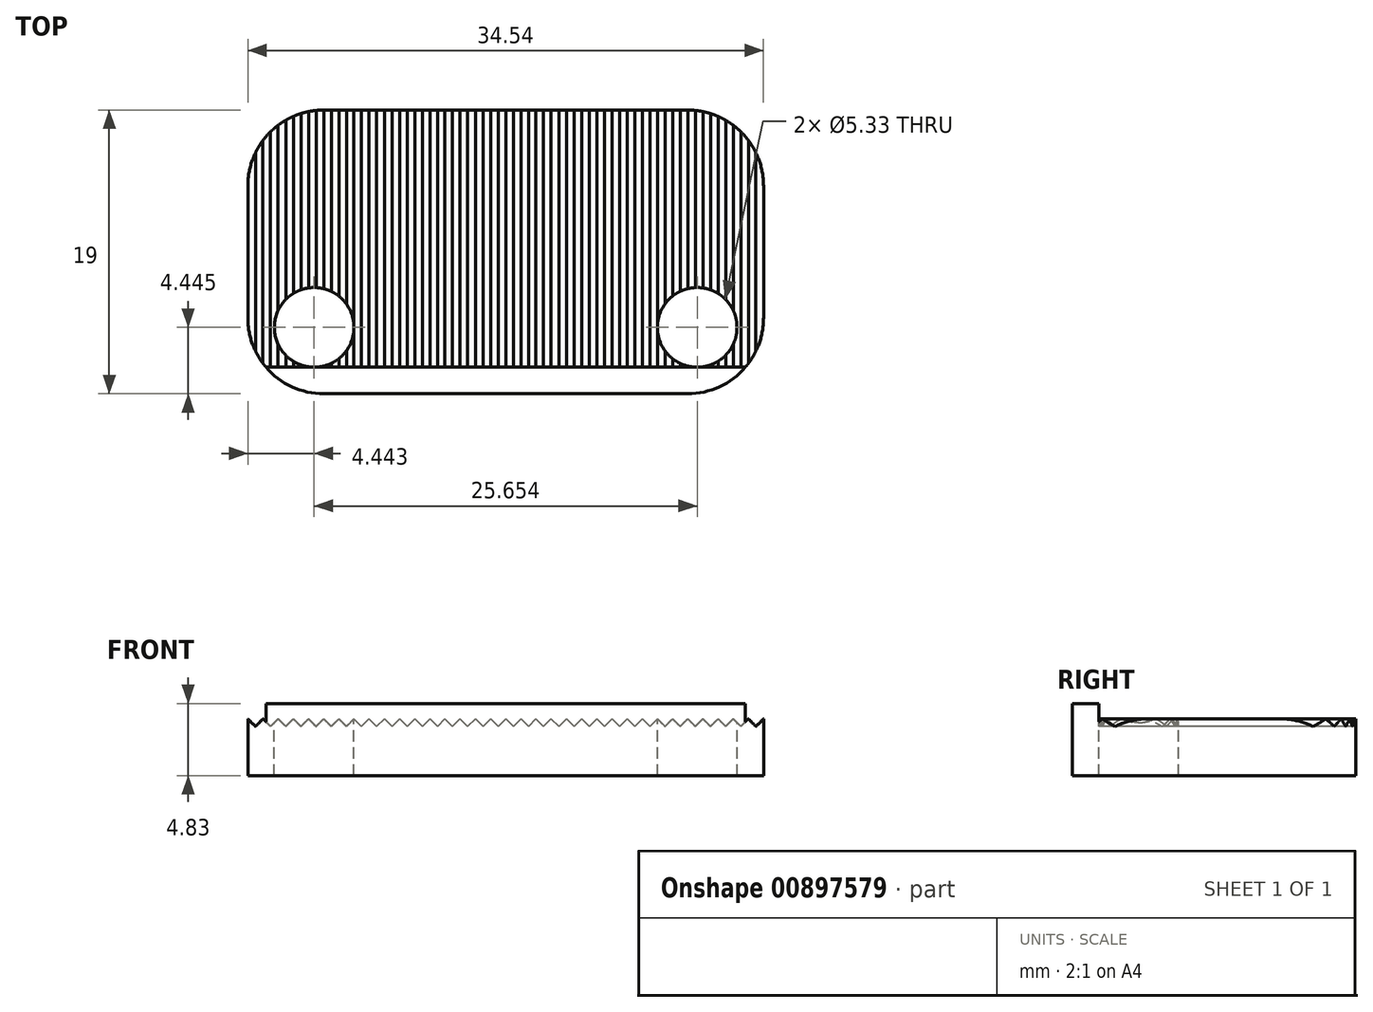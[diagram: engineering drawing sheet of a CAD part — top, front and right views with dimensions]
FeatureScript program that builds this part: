
annotation { "Feature Type Name" : "Feature", "Feature Type Description" : "" }
export const myFeature = defineFeature(function(context is Context, id is Id, definition is map)
    precondition{}
    {
        {
            var Q0;
            Q0=qCreatedBy(makeId("Top.planeOp"),FACE);
            var sketch = newSketch(context, id + "F0", { "sketchPlane" : qUnion([Q0])});
            skLineSegment(sketch, "E0.bottom", {"start": v(17.27, -9.5) * mm, "end": v(-17.27, -9.5) * mm});
            skLineSegment(sketch, "E0.top", {"start": v(17.27, 9.5) * mm, "end": v(-17.27, 9.5) * mm});
            skLineSegment(sketch, "E0.left", {"start": v(17.27, -9.5) * mm, "end": v(17.27, 9.5) * mm});
            skLineSegment(sketch, "E0.right", {"start": v(-17.27, -9.5) * mm, "end": v(-17.27, 9.5) * mm});
            skPoint(sketch, "E0.middle", {"position": v(0, 0) * mm});
            skSolve(sketch);
        }
        {
            var Q0;
            Q0=qSketchRegion(id+"F0",true);
            extrude(context, id + "F1", {"entities" : qUnion([Q0]), "depth" : 3.8 * mm, "offsetDistance" : 25.4 * mm});
        }
        {
            var Q0;
            Q0=makeQuery(id+"F1.opExtrude","SWEPT_FACE",FACE,{"disambiguationData":[OSD([sQuery(id+"F0.wireOp",EDGE,"E0.bottom")])]});
            var sketch = newSketch(context, id + "F2", { "sketchPlane" : qUnion([Q0])});
            skLineSegment(sketch, "E1", {"start": v(-16.27, 3.8) * mm, "end": v(-16.27, 3.06) * mm});
            skLineSegment(sketch, "E2", {"start": v(-16.27, 3.06) * mm, "end": v(-15.27, 3.06) * mm});
            skLineSegment(sketch, "E3", {"start": v(-15.27, 3.06) * mm, "end": v(-15.27, 3.8) * mm});
            skSolve(sketch);
        }
        {
            var Q0;
            Q0=makeQuery(id+"F1.opExtrude","CAP_FACE",FACE,{"disambiguationData":[OSD([sQuery(id+"F0.wireOp",EDGE,"E0.bottom"),sQuery(id+"F0.wireOp",EDGE,"E0.top"),sQuery(id+"F0.wireOp",EDGE,"E0.left"),sQuery(id+"F0.wireOp",EDGE,"E0.right")])],"isStart":false});
            var sketch = newSketch(context, id + "F3", { "sketchPlane" : qUnion([Q0])});
            skCircle(sketch, "E4", {"center": v(-12.83, -5.06) * mm, "radius": 2.67 * mm});
            skCircle(sketch, "E5", {"center": v(12.83, -5.06) * mm, "radius": 2.67 * mm});
            skSolve(sketch);
        }
        {
            var Q0;
            Q0=qSketchRegion(id+"F3",true);
            extrude(context, id + "F4", {"entities" : qUnion([Q0]), "operationType" : NewBodyOperationType.REMOVE, "oppositeDirection" : true, "depth" : 10.16 * mm, "offsetDistance" : 25.4 * mm});
        }
        {
            var Q0;
            Q0=makeQuery(id+"F1.opExtrude","SWEPT_FACE",FACE,{"disambiguationData":[OSD([sQuery(id+"F0.wireOp",EDGE,"E0.bottom")])]});
            var sketch = newSketch(context, id + "F5", { "sketchPlane" : qUnion([Q0])});
            skLineSegment(sketch, "E6", {"start": v(17.27, 3.8) * mm, "end": v(16.76, 3.3) * mm});
            skLineSegment(sketch, "E7", {"start": v(16.76, 3.3) * mm, "end": v(16.26, 3.81) * mm});
            skLineSegment(sketch, "E8.1.0.0", {"start": v(16.26, 3.8) * mm, "end": v(15.75, 3.3) * mm});
            skLineSegment(sketch, "E8.1.0.1", {"start": v(15.75, 3.3) * mm, "end": v(15.24, 3.81) * mm});
            skLineSegment(sketch, "E8.2.0.0", {"start": v(15.24, 3.81) * mm, "end": v(14.73, 3.3) * mm});
            skLineSegment(sketch, "E8.2.0.1", {"start": v(14.73, 3.3) * mm, "end": v(14.22, 3.81) * mm});
            skLineSegment(sketch, "E8.3.0.0", {"start": v(14.22, 3.8) * mm, "end": v(13.72, 3.3) * mm});
            skLineSegment(sketch, "E8.3.0.1", {"start": v(13.72, 3.3) * mm, "end": v(13.2, 3.81) * mm});
            skLineSegment(sketch, "E8.4.0.0", {"start": v(13.2, 3.8) * mm, "end": v(12.7, 3.3) * mm});
            skLineSegment(sketch, "E8.4.0.1", {"start": v(12.7, 3.3) * mm, "end": v(12.2, 3.81) * mm});
            skLineSegment(sketch, "E8.5.0.0", {"start": v(12.2, 3.8) * mm, "end": v(11.68, 3.3) * mm});
            skLineSegment(sketch, "E8.5.0.1", {"start": v(11.68, 3.3) * mm, "end": v(11.18, 3.81) * mm});
            skLineSegment(sketch, "E8.6.0.0", {"start": v(11.18, 3.8) * mm, "end": v(10.67, 3.3) * mm});
            skLineSegment(sketch, "E8.6.0.1", {"start": v(10.67, 3.3) * mm, "end": v(10.16, 3.81) * mm});
            skLineSegment(sketch, "E8.7.0.0", {"start": v(10.16, 3.8) * mm, "end": v(9.65, 3.3) * mm});
            skLineSegment(sketch, "E8.7.0.1", {"start": v(9.65, 3.3) * mm, "end": v(9.14, 3.81) * mm});
            skLineSegment(sketch, "E8.8.0.0", {"start": v(9.14, 3.8) * mm, "end": v(8.64, 3.3) * mm});
            skLineSegment(sketch, "E8.8.0.1", {"start": v(8.64, 3.3) * mm, "end": v(8.13, 3.81) * mm});
            skLineSegment(sketch, "E8.9.0.0", {"start": v(8.13, 3.8) * mm, "end": v(7.62, 3.3) * mm});
            skLineSegment(sketch, "E8.9.0.1", {"start": v(7.62, 3.3) * mm, "end": v(7.11, 3.81) * mm});
            skLineSegment(sketch, "E8.10.0.0", {"start": v(7.11, 3.8) * mm, "end": v(6.6, 3.3) * mm});
            skLineSegment(sketch, "E8.10.0.1", {"start": v(6.6, 3.3) * mm, "end": v(6.1, 3.81) * mm});
            skLineSegment(sketch, "E8.11.0.0", {"start": v(6.1, 3.8) * mm, "end": v(5.59, 3.3) * mm});
            skLineSegment(sketch, "E8.11.0.1", {"start": v(5.59, 3.3) * mm, "end": v(5.08, 3.81) * mm});
            skLineSegment(sketch, "E8.12.0.0", {"start": v(5.08, 3.8) * mm, "end": v(4.57, 3.3) * mm});
            skLineSegment(sketch, "E8.12.0.1", {"start": v(4.57, 3.3) * mm, "end": v(4.06, 3.81) * mm});
            skLineSegment(sketch, "E8.13.0.0", {"start": v(4.06, 3.8) * mm, "end": v(3.56, 3.3) * mm});
            skLineSegment(sketch, "E8.13.0.1", {"start": v(3.56, 3.3) * mm, "end": v(3.05, 3.81) * mm});
            skLineSegment(sketch, "E8.14.0.0", {"start": v(3.05, 3.8) * mm, "end": v(2.54, 3.3) * mm});
            skLineSegment(sketch, "E8.14.0.1", {"start": v(2.54, 3.3) * mm, "end": v(2.03, 3.81) * mm});
            skLineSegment(sketch, "E8.15.0.0", {"start": v(2.03, 3.8) * mm, "end": v(1.52, 3.3) * mm});
            skLineSegment(sketch, "E8.15.0.1", {"start": v(1.52, 3.3) * mm, "end": v(1.02, 3.8) * mm});
            skLineSegment(sketch, "E8.16.0.0", {"start": v(1.02, 3.8) * mm, "end": v(0.5, 3.3) * mm});
            skLineSegment(sketch, "E8.16.0.1", {"start": v(0.5, 3.3) * mm, "end": v(0, 3.81) * mm});
            skLineSegment(sketch, "E8.17.0.0", {"start": v(0, 3.8) * mm, "end": v(-0.5, 3.3) * mm});
            skLineSegment(sketch, "E8.17.0.1", {"start": v(-0.5, 3.3) * mm, "end": v(-1.02, 3.81) * mm});
            skLineSegment(sketch, "E8.18.0.0", {"start": v(-1.02, 3.8) * mm, "end": v(-1.52, 3.3) * mm});
            skLineSegment(sketch, "E8.18.0.1", {"start": v(-1.52, 3.3) * mm, "end": v(-2.03, 3.81) * mm});
            skLineSegment(sketch, "E8.19.0.0", {"start": v(-2.03, 3.8) * mm, "end": v(-2.54, 3.3) * mm});
            skLineSegment(sketch, "E8.19.0.1", {"start": v(-2.54, 3.3) * mm, "end": v(-3.05, 3.81) * mm});
            skLineSegment(sketch, "E8.direction1", {"start": v(16.76, 3.3) * mm, "end": v(15.75, 3.3) * mm, "construction": true});
            skLineSegment(sketch, "E9.0.20.0", {"start": v(-3.05, 3.8) * mm, "end": v(-3.56, 3.3) * mm});
            skLineSegment(sketch, "E9.3.20.0", {"start": v(-3.56, 3.3) * mm, "end": v(-4.06, 3.8) * mm});
            skLineSegment(sketch, "E9.0.21.0", {"start": v(-4.06, 3.8) * mm, "end": v(-4.57, 3.3) * mm});
            skLineSegment(sketch, "E9.3.21.0", {"start": v(-4.57, 3.3) * mm, "end": v(-5.08, 3.8) * mm});
            skLineSegment(sketch, "E9.0.22.0", {"start": v(-5.08, 3.8) * mm, "end": v(-5.59, 3.3) * mm});
            skLineSegment(sketch, "E9.3.22.0", {"start": v(-5.59, 3.3) * mm, "end": v(-6.1, 3.8) * mm});
            skLineSegment(sketch, "E9.0.23.0", {"start": v(-6.1, 3.8) * mm, "end": v(-6.6, 3.3) * mm});
            skLineSegment(sketch, "E9.3.23.0", {"start": v(-6.6, 3.3) * mm, "end": v(-7.11, 3.8) * mm});
            skLineSegment(sketch, "E9.0.24.0", {"start": v(-7.11, 3.8) * mm, "end": v(-7.62, 3.3) * mm});
            skLineSegment(sketch, "E9.3.24.0", {"start": v(-7.62, 3.3) * mm, "end": v(-8.13, 3.8) * mm});
            skLineSegment(sketch, "E9.0.25.0", {"start": v(-8.13, 3.8) * mm, "end": v(-8.64, 3.3) * mm});
            skLineSegment(sketch, "E9.3.25.0", {"start": v(-8.64, 3.3) * mm, "end": v(-9.14, 3.81) * mm});
            skLineSegment(sketch, "E9.0.26.0", {"start": v(-9.14, 3.8) * mm, "end": v(-9.65, 3.3) * mm});
            skLineSegment(sketch, "E9.3.26.0", {"start": v(-9.65, 3.3) * mm, "end": v(-10.16, 3.8) * mm});
            skLineSegment(sketch, "E9.0.27.0", {"start": v(-10.16, 3.8) * mm, "end": v(-10.67, 3.3) * mm});
            skLineSegment(sketch, "E9.3.27.0", {"start": v(-10.67, 3.3) * mm, "end": v(-11.18, 3.81) * mm});
            skLineSegment(sketch, "E9.0.28.0", {"start": v(-11.18, 3.8) * mm, "end": v(-11.68, 3.3) * mm});
            skLineSegment(sketch, "E9.3.28.0", {"start": v(-11.68, 3.3) * mm, "end": v(-12.2, 3.8) * mm});
            skLineSegment(sketch, "E9.0.29.0", {"start": v(-12.2, 3.8) * mm, "end": v(-12.7, 3.3) * mm});
            skLineSegment(sketch, "E9.3.29.0", {"start": v(-12.7, 3.3) * mm, "end": v(-13.2, 3.81) * mm});
            skLineSegment(sketch, "E9.0.30.0", {"start": v(-13.2, 3.8) * mm, "end": v(-13.72, 3.3) * mm});
            skLineSegment(sketch, "E9.3.30.0", {"start": v(-13.72, 3.3) * mm, "end": v(-14.22, 3.81) * mm});
            skLineSegment(sketch, "E10", {"start": v(17.27, 3.81) * mm, "end": v(-14.22, 3.81) * mm});
            skLineSegment(sketch, "E11.0.31.0", {"start": v(-14.22, 3.8) * mm, "end": v(-14.73, 3.3) * mm});
            skLineSegment(sketch, "E11.3.31.0", {"start": v(-14.73, 3.3) * mm, "end": v(-15.24, 3.8) * mm});
            skLineSegment(sketch, "E11.0.32.0", {"start": v(-15.24, 3.8) * mm, "end": v(-15.75, 3.3) * mm});
            skLineSegment(sketch, "E11.3.32.0", {"start": v(-15.75, 3.3) * mm, "end": v(-16.26, 3.8) * mm});
            skLineSegment(sketch, "E11.0.33.0", {"start": v(-16.26, 3.8) * mm, "end": v(-16.76, 3.3) * mm});
            skLineSegment(sketch, "E11.3.33.0", {"start": v(-16.76, 3.3) * mm, "end": v(-17.27, 3.8) * mm});
            skLineSegment(sketch, "E11.0.34.0", {"start": v(-17.27, 3.8) * mm, "end": v(-17.78, 3.3) * mm});
            skLineSegment(sketch, "E11.3.34.0", {"start": v(-17.78, 3.3) * mm, "end": v(-18.29, 3.81) * mm});
            skLineSegment(sketch, "E12", {"start": v(-18.29, 3.81) * mm, "end": v(-10.16, 3.81) * mm});
            skSolve(sketch);
        }
        {
            var Q0;
            Q0=qSketchRegion(id+"F5",true);
            extrude(context, id + "F6", {"entities" : qUnion([Q0]), "operationType" : NewBodyOperationType.REMOVE, "endBound" : BoundingType.THROUGH_ALL, "oppositeDirection" : true, "depth" : 25.4 * mm, "offsetDistance" : 25.4 * mm});
        }
        {
            var Q0;
            Q0=makeQuery(id+"F1.opExtrude","CAP_FACE",FACE,{"disambiguationData":[OSD([sQuery(id+"F0.wireOp",EDGE,"E0.bottom"),sQuery(id+"F0.wireOp",EDGE,"E0.top"),sQuery(id+"F0.wireOp",EDGE,"E0.left"),sQuery(id+"F0.wireOp",EDGE,"E0.right")])],"isStart":true});
            var sketch = newSketch(context, id + "F7", { "sketchPlane" : qUnion([Q0])});
            skLineSegment(sketch, "E13.bottom", {"start": v(17.27, 9.5) * mm, "end": v(-17.27, 9.5) * mm});
            skLineSegment(sketch, "E13.top", {"start": v(17.27, 7.72) * mm, "end": v(-17.27, 7.72) * mm});
            skLineSegment(sketch, "E13.left", {"start": v(17.27, 9.5) * mm, "end": v(17.27, 7.72) * mm});
            skLineSegment(sketch, "E13.right", {"start": v(-17.27, 9.5) * mm, "end": v(-17.27, 7.72) * mm});
            skSolve(sketch);
        }
        {
            var Q0;
            Q0 = qSketchRegion(id + "F7", true);
            extrude(context, id + "F8", {"entities" : qUnion([Q0]), "operationType" : NewBodyOperationType.ADD, "oppositeDirection" : true, "depth" : 4.83 * mm, "offsetDistance" : 25.4 * mm});
        }
        {
            var Q0;
            Q0=makeQuery(id+"F1.opExtrude","SWEPT_EDGE",EDGE,{"disambiguationData":[OSD([sQuery(id+"F0.wireOp",EDGE,"E0.bottom"),sQuery(id+"F0.wireOp",EDGE,"E0.left")])]});
            var Q1;
            Q1=makeQuery(id+"F1.opExtrude","SWEPT_EDGE",EDGE,{"disambiguationData":[OSD([sQuery(id+"F0.wireOp",EDGE,"E0.top"),sQuery(id+"F0.wireOp",EDGE,"E0.left")])]});
            var Q2;
            Q2=makeQuery(id+"F1.opExtrude","SWEPT_EDGE",EDGE,{"disambiguationData":[OSD([sQuery(id+"F0.wireOp",EDGE,"E0.top"),sQuery(id+"F0.wireOp",EDGE,"E0.right")])]});
            var Q3;
            Q3=makeQuery(id+"F1.opExtrude","SWEPT_EDGE",EDGE,{"disambiguationData":[OSD([sQuery(id+"F0.wireOp",EDGE,"E0.bottom"),sQuery(id+"F0.wireOp",EDGE,"E0.right")])]});
            fillet(context, id + "F9", {"entities" : qUnion([Q0, Q1, Q2, Q3]), "radius" : 5.08 * mm, "tangentPropagation" : true, "allowEdgeOverflow" : false});
        }
    });
